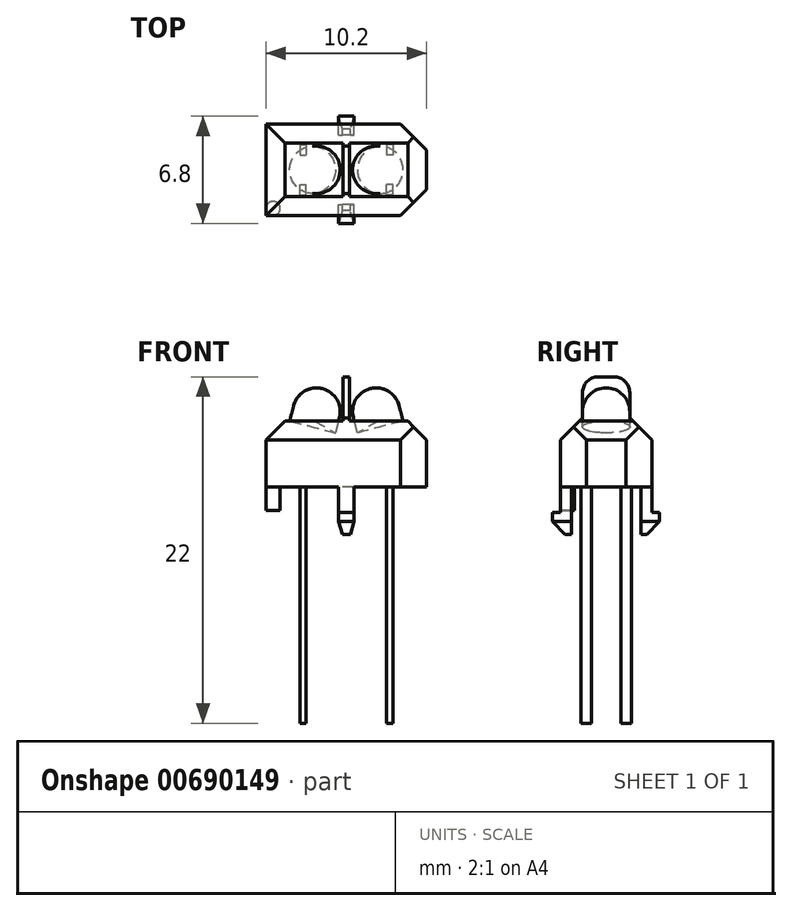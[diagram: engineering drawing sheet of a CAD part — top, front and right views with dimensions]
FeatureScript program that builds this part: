
annotation { "Feature Type Name" : "Feature", "Feature Type Description" : "" }
export const myFeature = defineFeature(function(context is Context, id is Id, definition is map)
    precondition{}
    {
        {
            var Q0;
            Q0=qCreatedBy(makeId("Front.planeOp"),FACE);
            var sketch = newSketch(context, id + "F0", { "sketchPlane" : qUnion([Q0])});
            skLineSegment(sketch, "E0", {"start": v(-5.1, 0) * mm, "end": v(-5.1, 3) * mm});
            skLineSegment(sketch, "E1", {"start": v(-5.1, 3) * mm, "end": v(-3.9, 4.2) * mm});
            skLineSegment(sketch, "E2", {"start": v(-3.9, 4.2) * mm, "end": v(-0.2, 4.2) * mm});
            skLineSegment(sketch, "E3", {"start": v(-0.2, 4.2) * mm, "end": v(-0.2, 7) * mm});
            skLineSegment(sketch, "E4", {"start": v(-0.2, 7) * mm, "end": v(0.2, 7) * mm});
            skLineSegment(sketch, "E5", {"start": v(0.2, 7) * mm, "end": v(0.2, 4.2) * mm});
            skLineSegment(sketch, "E6", {"start": v(0.2, 4.2) * mm, "end": v(3.9, 4.2) * mm});
            skLineSegment(sketch, "E7", {"start": v(3.9, 4.2) * mm, "end": v(5.1, 3) * mm});
            skLineSegment(sketch, "E8", {"start": v(5.1, 3) * mm, "end": v(5.1, 0) * mm});
            skLineSegment(sketch, "E9", {"start": v(5.1, 0) * mm, "end": v(0.5, 0) * mm});
            skLineSegment(sketch, "E10", {"start": v(-2.05, 4.2) * mm, "end": v(0, 12) * mm, "construction": true});
            skArc(sketch, "E11", {"start": v(-3.34, 5.18) * mm, "mid": v(-1.51, 6.25) * mm, "end": v(-0.44, 4.42) * mm});
            skLineSegment(sketch, "E12", {"start": v(-3.34, 5.18) * mm, "end": v(-3.6, 4.2) * mm});
            skLineSegment(sketch, "E13.MirrorCS", {"start": v(3.34, 5.18) * mm, "end": v(3.6, 4.2) * mm});
            skArc(sketch, "E14.MirrorCS", {"start": v(3.34, 5.18) * mm, "mid": v(1.51, 6.25) * mm, "end": v(0.44, 4.42) * mm});
            skLineSegment(sketch, "E15.MirrorCS", {"start": v(2.05, 4.2) * mm, "end": v(0, 12) * mm, "construction": true});
            skLineSegment(sketch, "E16", {"start": v(-0.5, 0) * mm, "end": v(-0.5, -2.2) * mm});
            skLineSegment(sketch, "E17", {"start": v(0.5, -2.2) * mm, "end": v(0.5, 0) * mm});
            skLineSegment(sketch, "E18", {"start": v(-0.5, -2.2) * mm, "end": v(-0.25, -3) * mm});
            skLineSegment(sketch, "E19", {"start": v(-0.25, -3) * mm, "end": v(0.25, -3) * mm});
            skLineSegment(sketch, "E20", {"start": v(0.25, -3) * mm, "end": v(0.5, -2.2) * mm});
            skLineSegment(sketch, "E21.trimOffspring", {"start": v(-0.5, 0) * mm, "end": v(-5.1, 0) * mm});
            skLineSegment(sketch, "E22", {"start": v(-2.05, 4.2) * mm, "end": v(-1.51, 6.25) * mm});
            skLineSegment(sketch, "E23", {"start": v(1.51, 6.25) * mm, "end": v(2.05, 4.2) * mm});
            skLineSegment(sketch, "E24", {"start": v(-3.34, 5.18) * mm, "end": v(-0.44, 4.42) * mm, "construction": true});
            skLineSegment(sketch, "E25", {"start": v(-0.44, 4.42) * mm, "end": v(-0.5, 4.2) * mm});
            skLineSegment(sketch, "E26", {"start": v(0.44, 4.42) * mm, "end": v(0.5, 4.2) * mm});
            skPoint(sketch, "E27", {"position": v(0, 9.5) * mm});
            skSolve(sketch);
        }
        {
            var Q0;
            {var subQ18=sQuery(id+"F0.wireOp",EDGE,"E0");Q0=makeQuery(id+"F0.imprint","IMPRINT",FACE,{"disambiguationData":[TD([[makeQuery(id+"F0.imprint","IMPRINT",EDGE,{"derivedFrom":subQ18}),-1.0]])]});}
            extrude(context, id + "F1", {"entities" : qUnion([Q0]), "endBound" : BoundingType.SYMMETRIC, "depth" : 10 * mm, "offsetDistance" : 25 * mm});
        }
        {
            var Q0;
            Q0=qCreatedBy(makeId("Right.planeOp"),FACE);
            var sketch = newSketch(context, id + "F2", { "sketchPlane" : qUnion([Q0])});
            skLineSegment(sketch, "E28", {"start": v(-0.5, 7) * mm, "end": v(0.5, 7) * mm});
            skLineSegment(sketch, "E29", {"start": v(1.5, 6) * mm, "end": v(1.5, 4.4) * mm});
            skLineSegment(sketch, "E30", {"start": v(1.5, 4.4) * mm, "end": v(2.9, 3) * mm});
            skLineSegment(sketch, "E31", {"start": v(2.9, 3) * mm, "end": v(2.9, -1.6) * mm});
            skLineSegment(sketch, "E32", {"start": v(2.9, -1.6) * mm, "end": v(3.4, -1.6) * mm});
            skLineSegment(sketch, "E33", {"start": v(3.4, -1.6) * mm, "end": v(3.4, -2.2) * mm});
            skLineSegment(sketch, "E34", {"start": v(3.4, -2.2) * mm, "end": v(2.6, -3) * mm});
            skLineSegment(sketch, "E35", {"start": v(2.6, -3) * mm, "end": v(2.2, -3) * mm});
            skLineSegment(sketch, "E36", {"start": v(2.2, -3) * mm, "end": v(2.2, 0) * mm});
            skLineSegment(sketch, "E37", {"start": v(2.2, 0) * mm, "end": v(-2.2, 0) * mm});
            skLineSegment(sketch, "E38.MirrorCS", {"start": v(-2.9, -1.6) * mm, "end": v(-3.4, -1.6) * mm});
            skLineSegment(sketch, "E39.MirrorCS", {"start": v(-1.5, 4.4) * mm, "end": v(-2.9, 3) * mm});
            skLineSegment(sketch, "E40.MirrorCS", {"start": v(-2.2, -3) * mm, "end": v(-2.2, 0) * mm});
            skLineSegment(sketch, "E41.MirrorCS", {"start": v(-2.9, 3) * mm, "end": v(-2.9, -1.6) * mm});
            skLineSegment(sketch, "E42.MirrorCS", {"start": v(-2.6, -3) * mm, "end": v(-2.2, -3) * mm});
            skLineSegment(sketch, "E43.MirrorCS", {"start": v(-3.4, -2.2) * mm, "end": v(-2.6, -3) * mm});
            skLineSegment(sketch, "E44.MirrorCS", {"start": v(-3.4, -1.6) * mm, "end": v(-3.4, -2.2) * mm});
            skLineSegment(sketch, "E45.MirrorCS", {"start": v(-1.5, 6) * mm, "end": v(-1.5, 4.4) * mm});
            skPoint(sketch, "E46.visualSharp", {"position": v(1.5, 7) * mm});
            skArc(sketch, "E46.filletArc", {"start": v(1.5, 6) * mm, "mid": v(1.2, 6.7) * mm, "end": v(0.5, 7) * mm});
            skPoint(sketch, "E47.visualSharp", {"position": v(-1.5, 7) * mm});
            skArc(sketch, "E47.filletArc", {"start": v(-0.5, 7) * mm, "mid": v(-1.2, 6.7) * mm, "end": v(-1.5, 6) * mm});
            skSolve(sketch);
        }
        {
            var Q0;
            Q0 = qSketchRegion(id + "F2", true);
            extrude(context, id + "F3", {"entities" : qUnion([Q0]), "operationType" : NewBodyOperationType.INTERSECT, "endBound" : BoundingType.SYMMETRIC, "depth" : 25 * mm, "offsetDistance" : 25 * mm});
        }
        {
            var Q0;
            Q0=makeQuery(id+"F3.boolean.opBoolean","MERGE",FACE,{"derivedFrom":[makeQuery(id+"F1.opExtrude","SWEPT_FACE",FACE,{"disambiguationData":[OSD([sQuery(id+"F0.wireOp",EDGE,"E9")])]}),makeQuery(id+"F1.opExtrude","SWEPT_FACE",FACE,{"disambiguationData":[OSD([sQuery(id+"F0.wireOp",EDGE,"E21.trimOffspring")])]})],"fromTools":[makeQuery(id+"F3.boolean.toolComplement.opBoolean","COPY",FACE,{"derivedFrom":makeQuery(id+"F3.opExtrude","SWEPT_FACE",FACE,{"disambiguationData":[OSD([sQuery(id+"F2.wireOp",EDGE,"E37")])]})})]});
            var sketch = newSketch(context, id + "F4", { "sketchPlane" : qUnion([Q0])});
            skCircle(sketch, "E48", {"center": v(-4.65, 2.45) * mm, "radius": 0.45 * mm});
            skLineSegment(sketch, "E49.bottom", {"start": v(-2.95, 1.6) * mm, "end": v(-2.55, 1.6) * mm});
            skLineSegment(sketch, "E49.top", {"start": v(-2.95, 0.94) * mm, "end": v(-2.55, 0.94) * mm});
            skLineSegment(sketch, "E49.left", {"start": v(-2.95, 1.6) * mm, "end": v(-2.95, 0.94) * mm});
            skLineSegment(sketch, "E49.right", {"start": v(-2.55, 1.6) * mm, "end": v(-2.55, 0.94) * mm});
            skLineSegment(sketch, "E50", {"start": v(-2.95, 1.27) * mm, "end": v(-2.55, 1.27) * mm, "construction": true});
            skLineSegment(sketch, "E51", {"start": v(-2.75, 1.6) * mm, "end": v(-2.75, 0.94) * mm, "construction": true});
            skLineSegment(sketch, "E52.MirrorCS", {"start": v(2.95, 1.6) * mm, "end": v(2.55, 1.6) * mm});
            skLineSegment(sketch, "E53.MirrorCS", {"start": v(2.55, 1.6) * mm, "end": v(2.55, 0.94) * mm});
            skLineSegment(sketch, "E54.MirrorCS", {"start": v(2.95, 1.6) * mm, "end": v(2.95, 0.94) * mm});
            skLineSegment(sketch, "E55.MirrorCS", {"start": v(2.95, 0.95) * mm, "end": v(2.55, 0.94) * mm});
            skLineSegment(sketch, "E56.MirrorCS", {"start": v(2.95, 1.27) * mm, "end": v(2.55, 1.27) * mm, "construction": true});
            skLineSegment(sketch, "E57.MirrorCS", {"start": v(2.75, 1.6) * mm, "end": v(2.75, 0.94) * mm, "construction": true});
            skLineSegment(sketch, "E58.MirrorCS", {"start": v(2.55, -1.6) * mm, "end": v(2.55, -0.95) * mm});
            skLineSegment(sketch, "E59.MirrorCS", {"start": v(2.95, -1.6) * mm, "end": v(2.55, -1.6) * mm});
            skLineSegment(sketch, "E60.MirrorCS", {"start": v(2.95, -0.95) * mm, "end": v(2.55, -0.94) * mm});
            skLineSegment(sketch, "E61.MirrorCS", {"start": v(2.75, -1.6) * mm, "end": v(2.75, -0.94) * mm, "construction": true});
            skLineSegment(sketch, "E62.MirrorCS", {"start": v(2.95, -1.6) * mm, "end": v(2.95, -0.95) * mm});
            skLineSegment(sketch, "E63.MirrorCS", {"start": v(2.95, -1.27) * mm, "end": v(2.55, -1.27) * mm, "construction": true});
            skLineSegment(sketch, "E64.MirrorCS", {"start": v(-2.95, -0.95) * mm, "end": v(-2.55, -0.94) * mm});
            skLineSegment(sketch, "E65.MirrorCS", {"start": v(-2.95, -1.6) * mm, "end": v(-2.55, -1.6) * mm});
            skLineSegment(sketch, "E66.MirrorCS", {"start": v(-2.95, -1.27) * mm, "end": v(-2.55, -1.27) * mm, "construction": true});
            skLineSegment(sketch, "E67.MirrorCS", {"start": v(-2.95, -1.6) * mm, "end": v(-2.95, -0.94) * mm});
            skLineSegment(sketch, "E68.MirrorCS", {"start": v(-2.55, -1.6) * mm, "end": v(-2.55, -0.95) * mm});
            skLineSegment(sketch, "E69.MirrorCS", {"start": v(-2.75, -1.6) * mm, "end": v(-2.75, -0.94) * mm, "construction": true});
            skLineSegment(sketch, "E70.0", {"start": v(5.1, 2.9) * mm, "end": v(5.1, -2.9) * mm});
            skLineSegment(sketch, "E71", {"start": v(5.1, 2.9) * mm, "end": v(3.45, 2.9) * mm});
            skLineSegment(sketch, "E72", {"start": v(3.45, 2.9) * mm, "end": v(5.1, 1.25) * mm});
            skLineSegment(sketch, "E73", {"start": v(5.1, -2.9) * mm, "end": v(3.45, -2.9) * mm});
            skLineSegment(sketch, "E74", {"start": v(3.45, -2.9) * mm, "end": v(5.1, -1.25) * mm});
            skSolve(sketch);
        }
        {
            var Q0;
            {var subQ0=sQuery(id+"F4.wireOp",EDGE,"E48");var subQ1=sQuery(id+"F0.wireOp",EDGE,"E21.trimOffspring");var subQ2=makeQuery(id+"F4.imprint","INTERSECT",VERTEX,{"derivedFrom":[makeQuery(id+"F1.opExtrude","SWEPT_EDGE",EDGE,{"disambiguationData":[OSD([sQuery(id+"F0.wireOp",EDGE,"E0"),subQ1])]}),subQ0]});Q0=makeQuery(id+"F4.imprint","IMPRINT",FACE,{"disambiguationData":[TD([[makeQuery(id+"F4.imprint","IMPRINT",EDGE,{"disambiguationData":[TD([[subQ2,1.0]])],"derivedFrom":subQ0}),1.0]])]});}
            extrude(context, id + "F5", {"entities" : qUnion([Q0]), "operationType" : NewBodyOperationType.ADD, "depth" : 1.5 * mm, "offsetDistance" : 25 * mm});
        }
        {
            var Q0;
            Q0=makeQuery(id+"F4.imprint","IMPRINT",FACE,{"disambiguationData":[TD([[makeQuery(id+"F4.imprint","IMPRINT",EDGE,{"derivedFrom":sQuery(id+"F4.wireOp",EDGE,"E49.bottom")}),-1.0]])]});
            var Q1;
            Q1=makeQuery(id+"F4.imprint","IMPRINT",FACE,{"disambiguationData":[TD([[makeQuery(id+"F4.imprint","IMPRINT",EDGE,{"derivedFrom":sQuery(id+"F4.wireOp",EDGE,"E64.MirrorCS")}),-1.0]])]});
            var Q2;
            Q2=makeQuery(id+"F4.imprint","IMPRINT",FACE,{"disambiguationData":[TD([[makeQuery(id+"F4.imprint","IMPRINT",EDGE,{"derivedFrom":sQuery(id+"F4.wireOp",EDGE,"E58.MirrorCS")}),-1.0]])]});
            var Q3;
            Q3=makeQuery(id+"F4.imprint","IMPRINT",FACE,{"disambiguationData":[TD([[makeQuery(id+"F4.imprint","IMPRINT",EDGE,{"derivedFrom":sQuery(id+"F4.wireOp",EDGE,"E52.MirrorCS")}),1.0]])]});
            extrude(context, id + "F6", {"entities" : qUnion([Q0, Q1, Q2, Q3]), "operationType" : NewBodyOperationType.ADD, "depth" : 15 * mm, "offsetDistance" : 25 * mm});
        }
        {
            var Q0;
            {var subQ0=sQuery(id+"F4.wireOp",EDGE,"E71");Q0=makeQuery(id+"F4.imprint","IMPRINT",FACE,{"disambiguationData":[TD([[makeQuery(id+"F4.imprint","IMPRINT",EDGE,{"derivedFrom":subQ0}),-1.0]])]});}
            var Q1;
            {var subQ0=sQuery(id+"F4.wireOp",EDGE,"E73");Q1=makeQuery(id+"F4.imprint","IMPRINT",FACE,{"disambiguationData":[TD([[makeQuery(id+"F4.imprint","IMPRINT",EDGE,{"derivedFrom":subQ0}),1.0]])]});}
            extrude(context, id + "F7", {"entities" : qUnion([Q0, Q1]), "operationType" : NewBodyOperationType.REMOVE, "endBound" : BoundingType.THROUGH_ALL, "oppositeDirection" : true, "depth" : 25 * mm, "offsetDistance" : 25 * mm});
        }
        {
            var Q0;
            {var subQ2=sQuery(id+"F0.wireOp",EDGE,"E12");Q0=makeQuery(id+"F0.imprint","IMPRINT",FACE,{"disambiguationData":[TD([[makeQuery(id+"F0.imprint","IMPRINT",EDGE,{"derivedFrom":subQ2}),1.0]])]});}
            var Q1;
            Q1=sQuery(id+"F0.wireOp",EDGE,"E10");
            revolve(context, id + "F8", {"surfaceOperationType" : NewSurfaceOperationType.NEW, "entities" : qUnion([Q0]), "axis" : qUnion([Q1]), "revolveType" : RevolveType.FULL});
        }
        {
            var Q0;
            {var subQ2=sQuery(id+"F0.wireOp",EDGE,"E13.MirrorCS");Q0=makeQuery(id+"F0.imprint","IMPRINT",FACE,{"disambiguationData":[TD([[makeQuery(id+"F0.imprint","IMPRINT",EDGE,{"derivedFrom":subQ2}),-1.0]])]});}
            var Q1;
            Q1=sQuery(id+"F0.wireOp",EDGE,"E23");
            revolve(context, id + "F9", {"surfaceOperationType" : NewSurfaceOperationType.NEW, "entities" : qUnion([Q0]), "axis" : qUnion([Q1]), "revolveType" : RevolveType.FULL});
        }
    });
